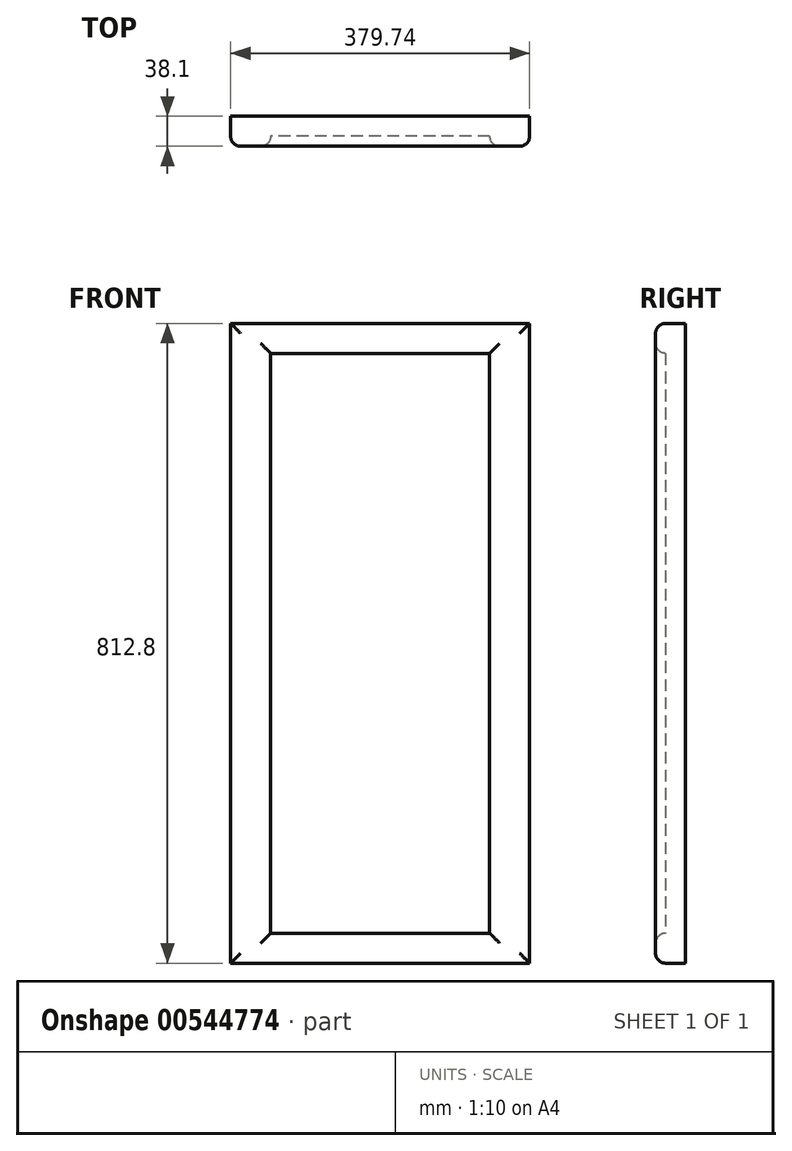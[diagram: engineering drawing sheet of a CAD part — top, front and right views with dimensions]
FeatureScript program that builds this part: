
annotation { "Feature Type Name" : "Feature", "Feature Type Description" : "" }
export const myFeature = defineFeature(function(context is Context, id is Id, definition is map)
    precondition{}
    {
        {
            var Q0;
            Q0=qCreatedBy(makeId("Front.planeOp"),FACE);
            var sketch = newSketch(context, id + "F0", { "sketchPlane" : qUnion([Q0])});
            skLineSegment(sketch, "E0.bottom", {"start": v(189.87, -406.4) * mm, "end": v(-189.87, -406.4) * mm});
            skLineSegment(sketch, "E0.top", {"start": v(189.87, 406.4) * mm, "end": v(-189.86, 406.4) * mm});
            skLineSegment(sketch, "E0.left", {"start": v(189.87, -406.4) * mm, "end": v(189.87, 406.4) * mm});
            skLineSegment(sketch, "E0.right", {"start": v(-189.87, -406.4) * mm, "end": v(-189.86, 406.4) * mm});
            skPoint(sketch, "E0.middle", {"position": v(0, 0) * mm});
            skSolve(sketch);
        }
        {
            var Q0;
            Q0 = qSketchRegion(id + "F0", true);
            extrude(context, id + "F1", {"entities" : qUnion([Q0]), "depth" : 25.4 * mm, "offsetDistance" : 25.4 * mm});
        }
        {
            var Q0;
            Q0=makeQuery(id+"F1.opExtrude","CAP_FACE",FACE,{"disambiguationData":[OSD([sQuery(id+"F0.wireOp",EDGE,"E0.bottom"),sQuery(id+"F0.wireOp",EDGE,"E0.top"),sQuery(id+"F0.wireOp",EDGE,"E0.left"),sQuery(id+"F0.wireOp",EDGE,"E0.right")])],"isStart":false});
            var sketch = newSketch(context, id + "F2", { "sketchPlane" : qUnion([Q0])});
            skLineSegment(sketch, "E1.bottom", {"start": v(139.06, 368.3) * mm, "end": v(-139.06, 368.3) * mm});
            skLineSegment(sketch, "E1.top", {"start": v(139.06, -368.3) * mm, "end": v(-139.06, -368.3) * mm});
            skLineSegment(sketch, "E1.left", {"start": v(139.06, 368.3) * mm, "end": v(139.06, -368.3) * mm});
            skLineSegment(sketch, "E1.right", {"start": v(-139.06, 368.3) * mm, "end": v(-139.06, -368.3) * mm});
            skPoint(sketch, "E1.middle", {"position": v(0, 0) * mm});
            skSolve(sketch);
        }
        {
            var Q0;
            Q0=makeQuery(id+"F2.imprint","IMPRINT",FACE,{"disambiguationData":[TD([[makeQuery(id+"F2.imprint","IMPRINT",EDGE,{"derivedFrom":sQuery(id+"F2.wireOp",EDGE,"E1.bottom")}),-1.0]])]});
            extrude(context, id + "F3", {"entities" : qUnion([Q0]), "operationType" : NewBodyOperationType.ADD, "depth" : 12.7 * mm, "offsetDistance" : 25.4 * mm});
        }
        {
            var Q0;
            Q0=makeQuery(id+"F3.opExtrude","CAP_EDGE",EDGE,{"disambiguationData":[OSD([sQuery(id+"F0.wireOp",EDGE,"E0.right")])],"isStart":false});
            var Q1;
            Q1=makeQuery(id+"F3.opExtrude","CAP_EDGE",EDGE,{"disambiguationData":[OSD([sQuery(id+"F0.wireOp",EDGE,"E0.bottom")])],"isStart":false});
            var Q2;
            Q2=makeQuery(id+"F3.opExtrude","CAP_EDGE",EDGE,{"disambiguationData":[OSD([sQuery(id+"F0.wireOp",EDGE,"E0.left")])],"isStart":false});
            var Q3;
            Q3=makeQuery(id+"F3.opExtrude","CAP_EDGE",EDGE,{"disambiguationData":[OSD([sQuery(id+"F0.wireOp",EDGE,"E0.top")])],"isStart":false});
            var Q4;
            Q4=makeQuery(id+"F3.opExtrude","CAP_EDGE",EDGE,{"disambiguationData":[OSD([sQuery(id+"F2.wireOp",EDGE,"E1.right")])],"isStart":false});
            var Q5;
            Q5=makeQuery(id+"F3.opExtrude","CAP_EDGE",EDGE,{"disambiguationData":[OSD([sQuery(id+"F2.wireOp",EDGE,"E1.top")])],"isStart":false});
            var Q6;
            Q6=makeQuery(id+"F3.opExtrude","CAP_EDGE",EDGE,{"disambiguationData":[OSD([sQuery(id+"F2.wireOp",EDGE,"E1.left")])],"isStart":false});
            var Q7;
            Q7=makeQuery(id+"F3.opExtrude","CAP_EDGE",EDGE,{"disambiguationData":[OSD([sQuery(id+"F2.wireOp",EDGE,"E1.bottom")])],"isStart":false});
            fillet(context, id + "F4", {"entities" : qUnion([Q0, Q1, Q2, Q3, Q4, Q5, Q6, Q7]), "radius" : 12.7 * mm, "tangentPropagation" : true, "allowEdgeOverflow" : false});
        }
    });
